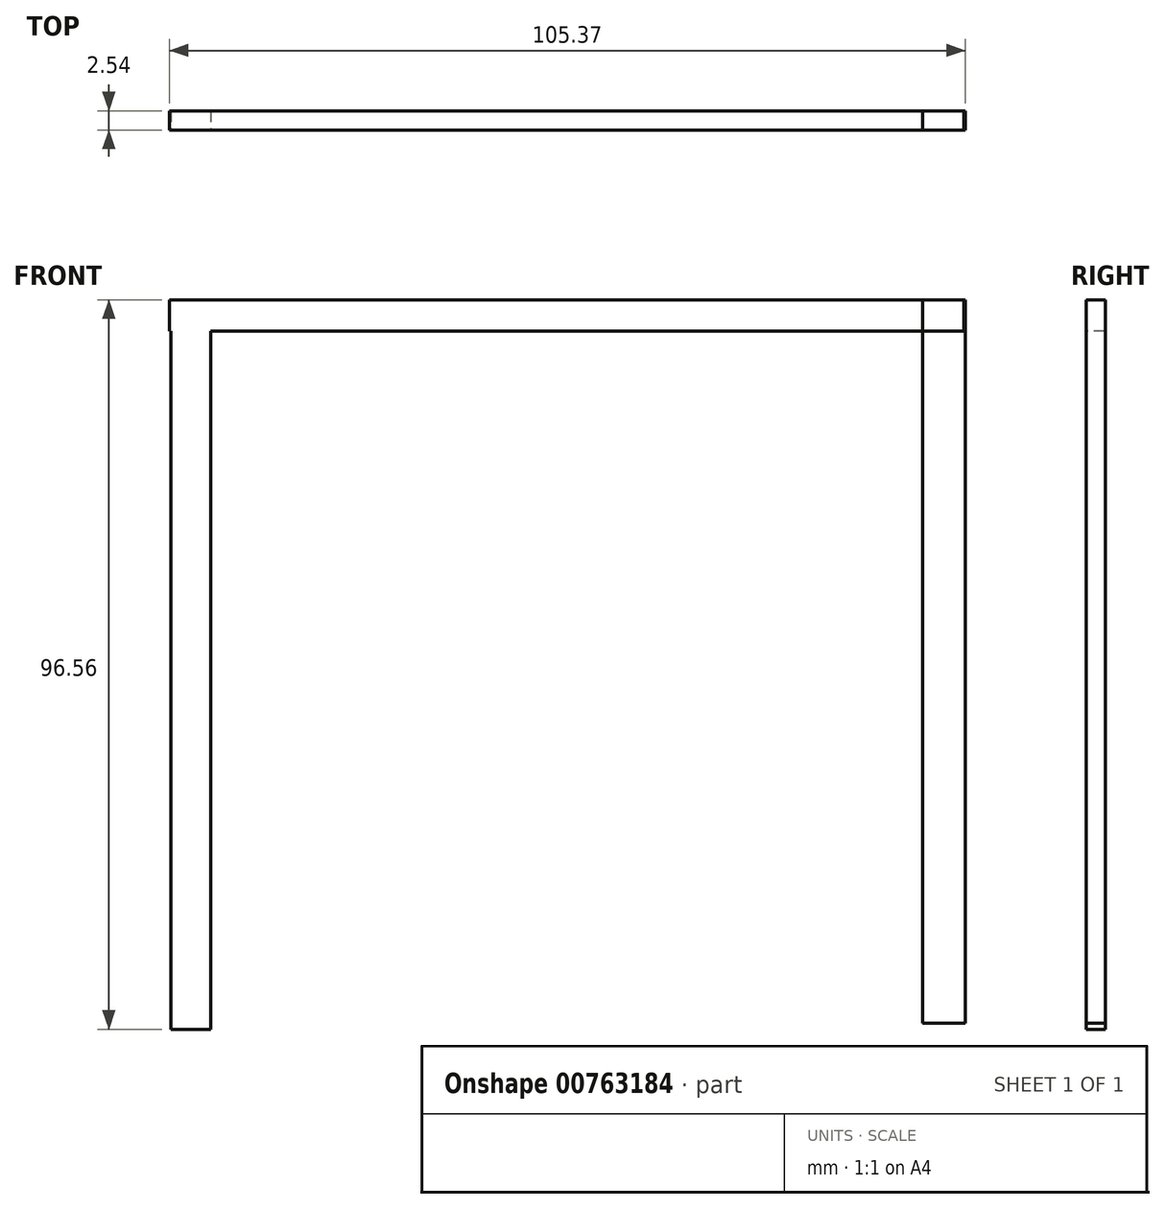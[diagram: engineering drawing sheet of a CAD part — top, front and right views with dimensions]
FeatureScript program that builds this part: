
annotation { "Feature Type Name" : "Feature", "Feature Type Description" : "" }
export const myFeature = defineFeature(function(context is Context, id is Id, definition is map)
    precondition{}
    {
        {
            var Q0;
            Q0=qCreatedBy(makeId("Front.planeOp"),FACE);
            var sketch = newSketch(context, id + "F0", { "sketchPlane" : qUnion([Q0])});
            skLineSegment(sketch, "E0.bottom", {"start": v(-49.85, 35.84) * mm, "end": v(-44.56, 35.84) * mm});
            skLineSegment(sketch, "E0.top", {"start": v(-49.85, -60.33) * mm, "end": v(-44.56, -60.33) * mm});
            skLineSegment(sketch, "E0.left", {"start": v(-49.85, 35.84) * mm, "end": v(-49.85, -60.33) * mm});
            skLineSegment(sketch, "E0.right", {"start": v(-44.56, 35.84) * mm, "end": v(-44.56, -60.33) * mm});
            skSolve(sketch);
        }
        {
            var Q0;
            Q0=makeQuery(id+"F0.imprint","IMPRINT",FACE,{"disambiguationData":[TD([[makeQuery(id+"F0.imprint","IMPRINT",EDGE,{"derivedFrom":sQuery(id+"F0.wireOp",EDGE,"E0.bottom")}),-1.0]])]});
            extrude(context, id + "F1", {"entities" : qUnion([Q0]), "depth" : 2.54 * mm, "offsetDistance" : 25.4 * mm});
        }
        {
            var Q0;
            Q0=qCreatedBy(makeId("Front.planeOp"),FACE);
            var sketch = newSketch(context, id + "F2", { "sketchPlane" : qUnion([Q0])});
            skLineSegment(sketch, "E1.bottom", {"start": v(-50.04, 36.23) * mm, "end": v(55.14, 36.23) * mm});
            skLineSegment(sketch, "E1.top", {"start": v(-50.04, 32.12) * mm, "end": v(55.14, 32.12) * mm});
            skLineSegment(sketch, "E1.left", {"start": v(-50.04, 36.23) * mm, "end": v(-50.04, 32.12) * mm});
            skLineSegment(sketch, "E1.right", {"start": v(55.14, 36.23) * mm, "end": v(55.14, 32.12) * mm});
            skSolve(sketch);
        }
        {
            var Q0;
            Q0=makeQuery(id+"F2.imprint","IMPRINT",FACE,{"disambiguationData":[TD([[makeQuery(id+"F2.imprint","IMPRINT",EDGE,{"derivedFrom":sQuery(id+"F2.wireOp",EDGE,"E1.bottom")}),-1.0]])]});
            extrude(context, id + "F3", {"entities" : qUnion([Q0]), "operationType" : NewBodyOperationType.ADD, "depth" : 2.54 * mm, "offsetDistance" : 25.4 * mm});
        }
        {
            var Q0;
            Q0=qCreatedBy(makeId("Front.planeOp"),FACE);
            var sketch = newSketch(context, id + "F4", { "sketchPlane" : qUnion([Q0])});
            skLineSegment(sketch, "E2.bottom", {"start": v(55.33, 36.23) * mm, "end": v(49.65, 36.23) * mm});
            skLineSegment(sketch, "E2.top", {"start": v(55.33, -59.54) * mm, "end": v(49.65, -59.54) * mm});
            skLineSegment(sketch, "E2.left", {"start": v(55.33, 36.23) * mm, "end": v(55.33, -59.54) * mm});
            skLineSegment(sketch, "E2.right", {"start": v(49.65, 36.23) * mm, "end": v(49.65, -59.54) * mm});
            skSolve(sketch);
        }
        {
            var Q0;
            Q0=makeQuery(id+"F4.imprint","IMPRINT",FACE,{"disambiguationData":[TD([[makeQuery(id+"F4.imprint","IMPRINT",EDGE,{"derivedFrom":sQuery(id+"F4.wireOp",EDGE,"E2.bottom")}),1.0]])]});
            extrude(context, id + "F5", {"entities" : qUnion([Q0]), "depth" : 2.54 * mm, "offsetDistance" : 25.4 * mm});
        }
    });
